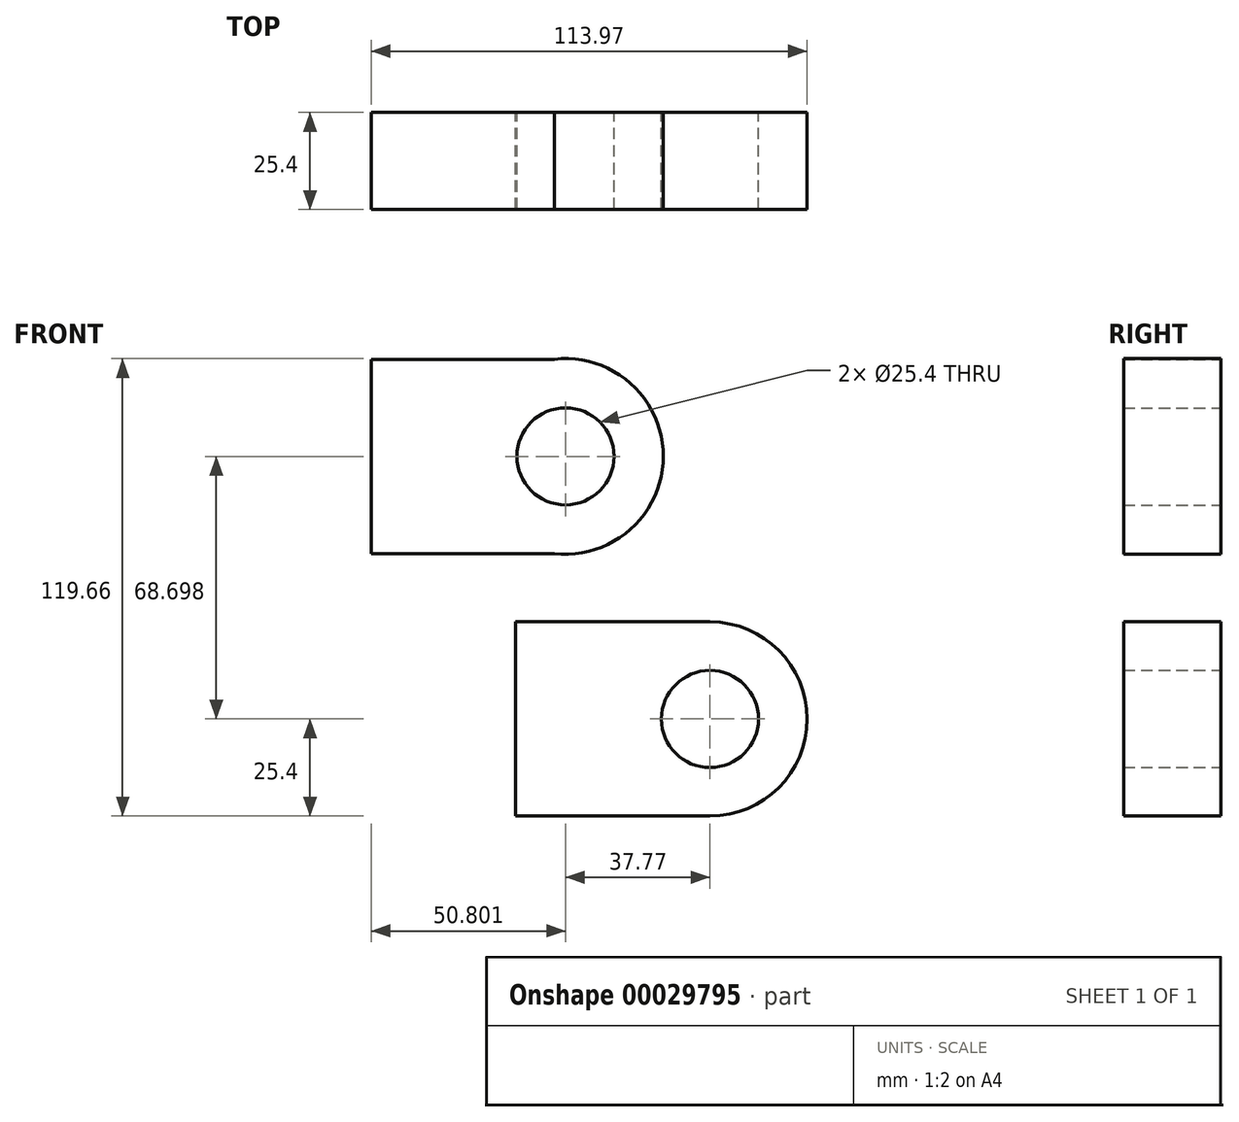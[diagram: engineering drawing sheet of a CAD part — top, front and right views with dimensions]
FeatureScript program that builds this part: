
annotation { "Feature Type Name" : "Feature", "Feature Type Description" : "" }
export const myFeature = defineFeature(function(context is Context, id is Id, definition is map)
    precondition{}
    {
        {
            var Q0;
            Q0=qCreatedBy(makeId("Front.planeOp"),FACE);
            var sketch = newSketch(context, id + "F0", { "sketchPlane" : qUnion([Q0])});
            skLineSegment(sketch, "E0.rect.bottom", {"start": v(-9.08, 0) * mm, "end": v(-59.88, 0) * mm});
            skLineSegment(sketch, "E0.rect.top", {"start": v(-9.08, 50.8) * mm, "end": v(-59.88, 50.8) * mm});
            skLineSegment(sketch, "E0.rect.right", {"start": v(-59.88, 0) * mm, "end": v(-59.88, 50.8) * mm});
            skPoint(sketch, "E0.rect.middle", {"position": v(-34.48, 25.4) * mm});
            skArc(sketch, "E1", {"start": v(-9.08, 0) * mm, "mid": v(16.32, 25.4) * mm, "end": v(-9.08, 50.8) * mm});
            skLineSegment(sketch, "E2", {"start": v(-9.08, 50.8) * mm, "end": v(-9.08, 0) * mm});
            skCircle(sketch, "E3", {"center": v(-9.08, 25.4) * mm, "radius": 12.7 * mm});
            skLineSegment(sketch, "E4", {"start": v(-9.08, 25.4) * mm, "end": v(-0.84, 35.07) * mm});
            skSolve(sketch);
        }
        {
            var Q0;
            Q0=qCreatedBy(makeId("Front.planeOp"),FACE);
            var sketch = newSketch(context, id + "F1", { "sketchPlane" : qUnion([Q0])});
            skLineSegment(sketch, "E5.rect.bottom", {"start": v(-46.85, 68.7) * mm, "end": v(-97.65, 68.7) * mm});
            skLineSegment(sketch, "E5.rect.top", {"start": v(-46.85, 119.5) * mm, "end": v(-97.65, 119.5) * mm});
            skLineSegment(sketch, "E5.rect.right", {"start": v(-97.65, 68.7) * mm, "end": v(-97.65, 119.5) * mm});
            skPoint(sketch, "E5.rect.middle", {"position": v(-72.25, 94.1) * mm});
            skArc(sketch, "E6", {"start": v(-49.74, 68.7) * mm, "mid": v(-21.29, 94.1) * mm, "end": v(-49.74, 119.5) * mm});
            skLineSegment(sketch, "E7", {"start": v(-49.74, 119.5) * mm, "end": v(-49.74, 68.7) * mm});
            skCircle(sketch, "E8", {"center": v(-46.85, 94.1) * mm, "radius": 12.7 * mm});
            skLineSegment(sketch, "E9", {"start": v(-46.85, 94.1) * mm, "end": v(-40.91, 105.33) * mm});
            skSolve(sketch);
        }
        {
            var Q0;
            {var subQ9=sQuery(id+"F1.wireOp",EDGE,"E5.rect.right");Q0=makeQuery(id+"F1.imprint","IMPRINT",FACE,{"disambiguationData":[TD([[makeQuery(id+"F1.imprint","IMPRINT",EDGE,{"derivedFrom":subQ9}),-1.0]])]});}
            var Q1;
            {var subQ5=sQuery(id+"F1.wireOp",EDGE,"E6");Q1=makeQuery(id+"F1.imprint","IMPRINT",FACE,{"disambiguationData":[TD([[makeQuery(id+"F1.imprint","IMPRINT",EDGE,{"derivedFrom":subQ5}),1.0]])]});}
            var Q2;
            {var subQ6=sQuery(id+"F0.wireOp",EDGE,"E0.rect.bottom");Q2=makeQuery(id+"F0.imprint","IMPRINT",FACE,{"disambiguationData":[TD([[makeQuery(id+"F0.imprint","IMPRINT",EDGE,{"derivedFrom":subQ6}),-1.0]])]});}
            var Q3;
            {var subQ5=sQuery(id+"F0.wireOp",EDGE,"E1");Q3=makeQuery(id+"F0.imprint","IMPRINT",FACE,{"disambiguationData":[TD([[makeQuery(id+"F0.imprint","IMPRINT",EDGE,{"derivedFrom":subQ5}),1.0]])]});}
            extrude(context, id + "F2", {"entities" : qUnion([Q0, Q1, Q2, Q3]), "depth" : 25.4 * mm});
        }
    });
